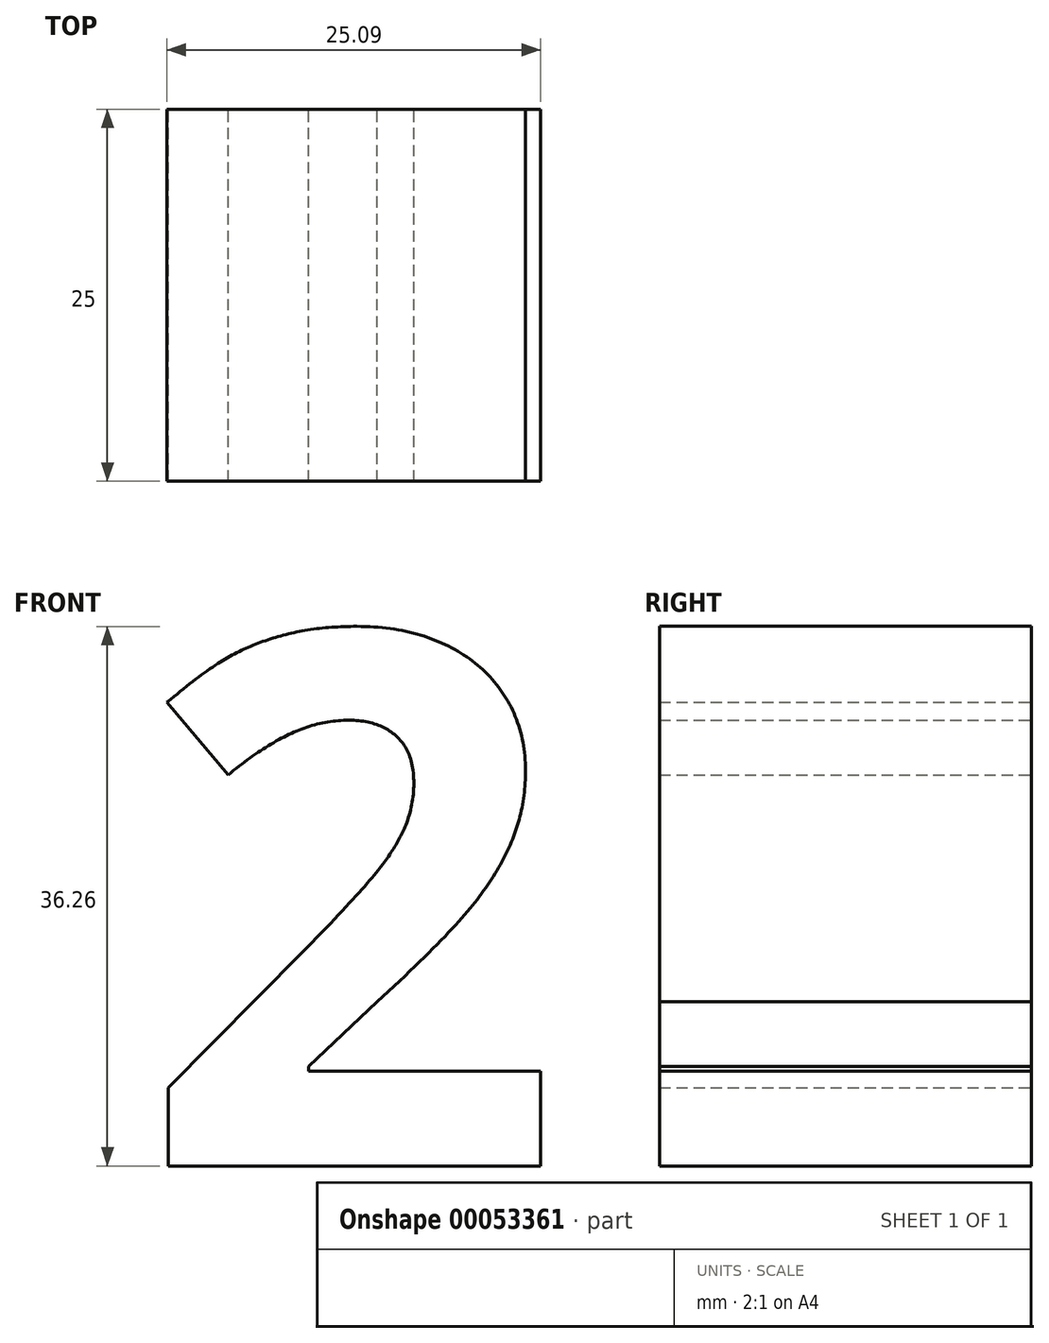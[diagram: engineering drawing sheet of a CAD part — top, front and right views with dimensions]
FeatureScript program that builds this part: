
annotation { "Feature Type Name" : "Feature", "Feature Type Description" : "" }
export const myFeature = defineFeature(function(context is Context, id is Id, definition is map)
    precondition{}
    {
        {
            var Q0;
            Q0=qCreatedBy(makeId("Front.planeOp"),FACE);
            var sketch = newSketch(context, id + "F0", { "sketchPlane" : qUnion([Q0])});
            skText(sketch, "E0", { "text": "2", "fontName": "OpenSans-Bold.ttf"});
            const initialGuessF0  = {"E0": [-0.01098, -0.02364, 1, 0, 0.03606]};
            skSetInitialGuess(sketch, initialGuessF0);
            skSolve(sketch);
        }
        {
            var Q0;
            Q0 = qSketchRegion(id + "F0", true);
            extrude(context, id + "F1", {"entities" : qUnion([Q0]), "depth" : 25 * mm});
        }
    });
